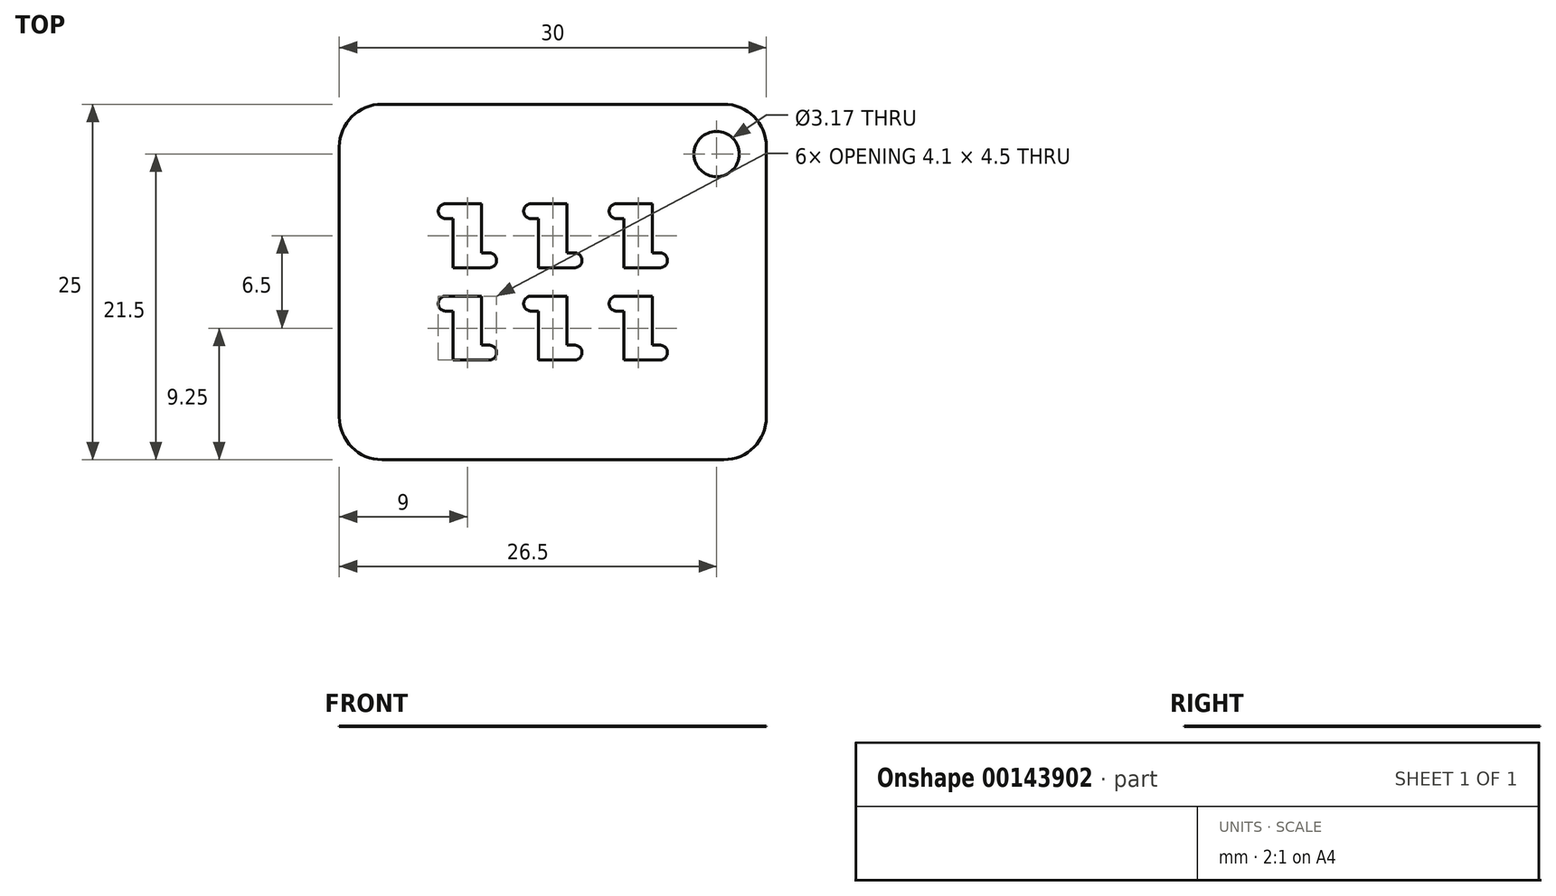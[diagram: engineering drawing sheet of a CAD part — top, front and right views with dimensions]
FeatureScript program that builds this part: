
annotation { "Feature Type Name" : "Feature", "Feature Type Description" : "" }
export const myFeature = defineFeature(function(context is Context, id is Id, definition is map)
    precondition{}
    {
        {
            var Q0;
            Q0=qCreatedBy(makeId("Top.planeOp"),FACE);
            var sketch = newSketch(context, id + "F0", { "sketchPlane" : qUnion([Q0])});
            skPoint(sketch, "E0.middle", {"position": v(0, 0) * mm});
            skLineSegment(sketch, "E1.bottom", {"start": v(1, 5.5) * mm, "end": v(-1, 5.5) * mm});
            skLineSegment(sketch, "E1.top", {"start": v(1, 1) * mm, "end": v(-1, 1) * mm});
            skLineSegment(sketch, "E1.left", {"start": v(1, 5.5) * mm, "end": v(1, 2.05) * mm});
            skPoint(sketch, "E1.middle", {"position": v(0, 3.25) * mm});
            skLineSegment(sketch, "E2.bottom", {"start": v(1, -5.5) * mm, "end": v(-1, -5.5) * mm});
            skLineSegment(sketch, "E2.top", {"start": v(1, -1) * mm, "end": v(-1, -1) * mm});
            skLineSegment(sketch, "E2.right", {"start": v(-1, -5.5) * mm, "end": v(-1, -2.05) * mm});
            skPoint(sketch, "E2.middle", {"position": v(0, -3.25) * mm});
            skArc(sketch, "E3", {"start": v(-1.53, 5.5) * mm, "mid": v(-2.05, 4.97) * mm, "end": v(-1.53, 4.45) * mm});
            skArc(sketch, "E4", {"start": v(1.53, 1) * mm, "mid": v(2.05, 1.52) * mm, "end": v(1.52, 2.05) * mm});
            skArc(sketch, "E5", {"start": v(-1.52, -1) * mm, "mid": v(-2.05, -1.52) * mm, "end": v(-1.52, -2.05) * mm});
            skArc(sketch, "E6", {"start": v(1.53, -5.5) * mm, "mid": v(2.05, -4.97) * mm, "end": v(1.53, -4.45) * mm});
            skLineSegment(sketch, "E7", {"start": v(-1, 5.5) * mm, "end": v(-1.53, 5.5) * mm});
            skLineSegment(sketch, "E8", {"start": v(-1, 4.45) * mm, "end": v(-1.53, 4.45) * mm});
            skLineSegment(sketch, "E9", {"start": v(1, 1) * mm, "end": v(1.52, 1) * mm});
            skLineSegment(sketch, "E10", {"start": v(-1, -1) * mm, "end": v(-1.52, -1) * mm});
            skLineSegment(sketch, "E11", {"start": v(1, -5.5) * mm, "end": v(1.53, -5.5) * mm});
            skLineSegment(sketch, "E12", {"start": v(1, 2.05) * mm, "end": v(1.52, 2.05) * mm});
            skLineSegment(sketch, "E13", {"start": v(-1, -2.05) * mm, "end": v(-1.52, -2.05) * mm});
            skLineSegment(sketch, "E14", {"start": v(1, -4.45) * mm, "end": v(1.53, -4.45) * mm});
            skLineSegment(sketch, "E15.trimOffspring", {"start": v(-1, 4.45) * mm, "end": v(-1, 1) * mm});
            skLineSegment(sketch, "E16.trimOffspring", {"start": v(1, -4.45) * mm, "end": v(1, -1) * mm});
            skPoint(sketch, "E17.1.0.0", {"position": v(6, 0) * mm});
            skLineSegment(sketch, "E17.1.0.1", {"start": v(7, 1) * mm, "end": v(5, 1) * mm});
            skPoint(sketch, "E17.1.0.2", {"position": v(6, -3.25) * mm});
            skLineSegment(sketch, "E17.1.0.3", {"start": v(7, 5.5) * mm, "end": v(5, 5.5) * mm});
            skLineSegment(sketch, "E17.1.0.4", {"start": v(7, 5.5) * mm, "end": v(7, 2.05) * mm});
            skLineSegment(sketch, "E17.1.0.5", {"start": v(7, -5.5) * mm, "end": v(5, -5.5) * mm});
            skLineSegment(sketch, "E17.1.0.6", {"start": v(7, -1) * mm, "end": v(5, -1) * mm});
            skPoint(sketch, "E17.1.0.7", {"position": v(6, 3.25) * mm});
            skLineSegment(sketch, "E17.1.0.8", {"start": v(5, 4.45) * mm, "end": v(5, 1) * mm});
            skLineSegment(sketch, "E17.1.0.9", {"start": v(5, -5.5) * mm, "end": v(5, -2.05) * mm});
            skLineSegment(sketch, "E17.1.0.10", {"start": v(7, -4.45) * mm, "end": v(7, -1) * mm});
            skArc(sketch, "E17.1.0.11", {"start": v(4.48, -1) * mm, "mid": v(3.95, -1.52) * mm, "end": v(4.48, -2.05) * mm});
            skArc(sketch, "E17.1.0.12", {"start": v(4.47, 5.5) * mm, "mid": v(3.95, 4.97) * mm, "end": v(4.47, 4.45) * mm});
            skLineSegment(sketch, "E17.1.0.13", {"start": v(5, 4.45) * mm, "end": v(4.47, 4.45) * mm});
            skLineSegment(sketch, "E17.1.0.14", {"start": v(5, -2.05) * mm, "end": v(4.48, -2.05) * mm});
            skLineSegment(sketch, "E17.1.0.15", {"start": v(5, 5.5) * mm, "end": v(4.47, 5.5) * mm});
            skArc(sketch, "E17.1.0.16", {"start": v(7.53, -5.5) * mm, "mid": v(8.05, -4.97) * mm, "end": v(7.53, -4.45) * mm});
            skLineSegment(sketch, "E17.1.0.17", {"start": v(5, -1) * mm, "end": v(4.48, -1) * mm});
            skLineSegment(sketch, "E17.1.0.18", {"start": v(7, 2.05) * mm, "end": v(7.53, 2.05) * mm});
            skLineSegment(sketch, "E17.1.0.19", {"start": v(7, -4.45) * mm, "end": v(7.53, -4.45) * mm});
            skLineSegment(sketch, "E17.1.0.20", {"start": v(7, 1) * mm, "end": v(7.53, 1) * mm});
            skLineSegment(sketch, "E17.1.0.21", {"start": v(7, -5.5) * mm, "end": v(7.53, -5.5) * mm});
            skArc(sketch, "E17.1.0.22", {"start": v(7.53, 1) * mm, "mid": v(8.05, 1.52) * mm, "end": v(7.53, 2.05) * mm});
            skPoint(sketch, "E17.2.0.0", {"position": v(12, 0) * mm});
            skLineSegment(sketch, "E17.2.0.1", {"start": v(13, 1) * mm, "end": v(11, 1) * mm});
            skPoint(sketch, "E17.2.0.2", {"position": v(12, -3.25) * mm});
            skLineSegment(sketch, "E17.2.0.3", {"start": v(13, 5.5) * mm, "end": v(11, 5.5) * mm});
            skLineSegment(sketch, "E17.2.0.4", {"start": v(13, 5.5) * mm, "end": v(13, 2.05) * mm});
            skLineSegment(sketch, "E17.2.0.5", {"start": v(13, -5.5) * mm, "end": v(11, -5.5) * mm});
            skLineSegment(sketch, "E17.2.0.6", {"start": v(13, -1) * mm, "end": v(11, -1) * mm});
            skPoint(sketch, "E17.2.0.7", {"position": v(12, 3.25) * mm});
            skLineSegment(sketch, "E17.2.0.8", {"start": v(11, 4.45) * mm, "end": v(11, 1) * mm});
            skLineSegment(sketch, "E17.2.0.9", {"start": v(11, -5.5) * mm, "end": v(11, -2.05) * mm});
            skLineSegment(sketch, "E17.2.0.10", {"start": v(13, -4.45) * mm, "end": v(13, -1) * mm});
            skArc(sketch, "E17.2.0.11", {"start": v(10.48, -1) * mm, "mid": v(9.95, -1.52) * mm, "end": v(10.48, -2.05) * mm});
            skArc(sketch, "E17.2.0.12", {"start": v(10.47, 5.5) * mm, "mid": v(9.95, 4.97) * mm, "end": v(10.47, 4.45) * mm});
            skLineSegment(sketch, "E17.2.0.13", {"start": v(11, 4.45) * mm, "end": v(10.47, 4.45) * mm});
            skLineSegment(sketch, "E17.2.0.14", {"start": v(11, -2.05) * mm, "end": v(10.48, -2.05) * mm});
            skLineSegment(sketch, "E17.2.0.15", {"start": v(11, 5.5) * mm, "end": v(10.47, 5.5) * mm});
            skArc(sketch, "E17.2.0.16", {"start": v(13.53, -5.5) * mm, "mid": v(14.05, -4.97) * mm, "end": v(13.53, -4.45) * mm});
            skLineSegment(sketch, "E17.2.0.17", {"start": v(11, -1) * mm, "end": v(10.47, -1) * mm});
            skLineSegment(sketch, "E17.2.0.18", {"start": v(13, 2.05) * mm, "end": v(13.53, 2.05) * mm});
            skLineSegment(sketch, "E17.2.0.19", {"start": v(13, -4.45) * mm, "end": v(13.53, -4.45) * mm});
            skLineSegment(sketch, "E17.2.0.20", {"start": v(13, 1) * mm, "end": v(13.53, 1) * mm});
            skLineSegment(sketch, "E17.2.0.21", {"start": v(13, -5.5) * mm, "end": v(13.53, -5.5) * mm});
            skArc(sketch, "E17.2.0.22", {"start": v(13.53, 1) * mm, "mid": v(14.05, 1.52) * mm, "end": v(13.53, 2.05) * mm});
            skLineSegment(sketch, "E17.direction1", {"start": v(-1, -5.5) * mm, "end": v(5, -5.5) * mm, "construction": true});
            skLineSegment(sketch, "E18.bottom", {"start": v(18, -12.5) * mm, "end": v(-6, -12.5) * mm});
            skLineSegment(sketch, "E18.top", {"start": v(18, 12.5) * mm, "end": v(-6, 12.5) * mm});
            skLineSegment(sketch, "E18.left", {"start": v(21, -9.5) * mm, "end": v(21, 9.5) * mm});
            skLineSegment(sketch, "E18.right", {"start": v(-9, -9.5) * mm, "end": v(-9, 9.5) * mm});
            skPoint(sketch, "E19.visualSharp", {"position": v(-9, 12.5) * mm});
            skArc(sketch, "E19.filletArc", {"start": v(-6, 12.5) * mm, "mid": v(-8.12, 11.62) * mm, "end": v(-9, 9.5) * mm});
            skPoint(sketch, "E20.visualSharp", {"position": v(21, 12.5) * mm});
            skArc(sketch, "E20.filletArc", {"start": v(21, 9.5) * mm, "mid": v(20.12, 11.62) * mm, "end": v(18, 12.5) * mm});
            skPoint(sketch, "E21.visualSharp", {"position": v(-9, -12.5) * mm});
            skArc(sketch, "E21.filletArc", {"start": v(-9, -9.5) * mm, "mid": v(-8.12, -11.62) * mm, "end": v(-6, -12.5) * mm});
            skPoint(sketch, "E22.visualSharp", {"position": v(21, -12.5) * mm});
            skArc(sketch, "E22.filletArc", {"start": v(18, -12.5) * mm, "mid": v(20.12, -11.62) * mm, "end": v(21, -9.5) * mm});
            skCircle(sketch, "E23", {"center": v(17.5, 9) * mm, "radius": 1.59 * mm});
            skSolve(sketch);
        }
        {
            var Q0;
            Q0=makeQuery(id+"F0.imprint","IMPRINT",FACE,{"disambiguationData":[TD([[makeQuery(id+"F0.imprint","IMPRINT",EDGE,{"derivedFrom":sQuery(id+"F0.wireOp",EDGE,"E1.bottom")}),-1.0]])]});
            extrude(context, id + "F1", {"entities" : qUnion([Q0]), "depth" : 1 / 406.4 * mm});
        }
    });
